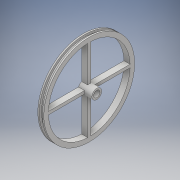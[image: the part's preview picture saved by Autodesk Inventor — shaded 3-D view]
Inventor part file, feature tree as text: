
AUTODESK INVENTOR PART (.ipt)
format: ipt  version: 2018 (Build 220112000, 112)  size: 168,448 bytes
history: native  units: mm
features: extrude x7, sketch x7, pattern_circular x1
ambient origin geometry x8: Origin, YZ Plane, XZ Plane, XY Plane, X Axis, Y Axis, Z Axis, Center Point
bodies: Solid1 (feature_tree)
feature tree (15):
  extrude  "Extrusion1"  Depth=2.0mm TaperAngle=0.0deg
  extrude  "Extrusion2"  Depth=1.0mm TaperAngle=0.0deg
  extrude  "Extrusion3"  Depth=1.0mm TaperAngle=0.0deg
  extrude  "Extrusion4"  Depth=10.0mm TaperAngle=0.0deg
  extrude  "Extrusion5"  Depth=6.5mm
  extrude  "Extrusion6"  Depth=1.0mm
  pattern_circular  "Circular Pattern1"  [2 undecoded]
  extrude  "Extrusion7"  Depth=5.0mm TaperAngle=360.0deg
  sketch  "Sketch1"  dims[d0=57.0mm d1=2.0mm d2=0.0mm]
  sketch  "Sketch2"  dims[d3=60.0mm d4=1.0mm d5=0.0mm]
  sketch  "Sketch3"  dims[d6=60.0mm d7=1.0mm d8=0.0mm]
  sketch  "Sketch4"  dims[d9=54.0mm d10=10.0mm d11=0.0mm]
  sketch  "Sketch5"  dims[d12=4.25mm d13=6.5mm]
  sketch  "Sketch6"  dims[d14=4.0mm d15=0.0mm d16=1.0mm]
  sketch  "Sketch7"  dims[d17=2.0mm d18=4.0mm d19=0.0mm d20=40.0mm d21=360.0deg d23=5.0mm d24=0.0mm]
note: 2 required parameter values undecoded (feature->parameter linkage not recoverable at this tier; creation-order binding heuristic only, values carry confidence <= 0.55)
